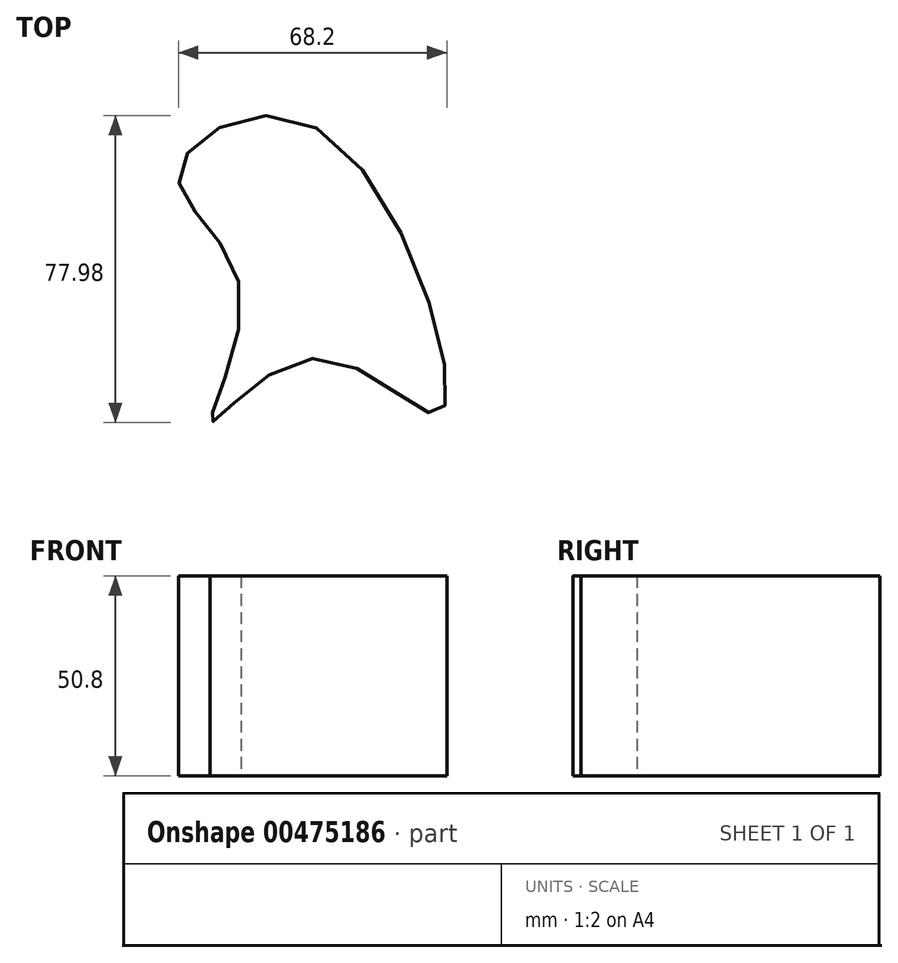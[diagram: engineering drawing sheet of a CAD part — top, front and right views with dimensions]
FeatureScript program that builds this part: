
annotation { "Feature Type Name" : "Feature", "Feature Type Description" : "" }
export const myFeature = defineFeature(function(context is Context, id is Id, definition is map)
    precondition{}
    {
        {
            var Q0;
            Q0=qCreatedBy(makeId("Top.planeOp"),FACE);
            var sketch = newSketch(context, id + "F0", { "sketchPlane" : qUnion([Q0])});
            skFitSpline(sketch, "E0", {"points": [v(0, 40.57) * mm, v(-35.01, 29.09) * mm, v(-19.45, 0) * mm, v(-26.86, -34.27) * mm, v(0, -17.97) * mm, v(31.68, -31.68) * mm, v(0, 40.57) * mm]});
            skSolve(sketch);
        }
        {
            var Q0;
            Q0=makeQuery(id+"F0.imprint","IMPRINT",FACE,{"disambiguationData":[TD([[makeQuery(id+"F0.imprint","IMPRINT",EDGE,{"derivedFrom":sQuery(id+"F0.wireOp",EDGE,"E0")}),1.0]])]});
            extrude(context, id + "F1", {"entities" : qUnion([Q0]), "depth" : 50.8 * mm});
        }
    });
